# Revit family: SBS20BL
name_source: partatom
category: Generic Models
units: mm (PartAtom-declared; Revit-internal decimal feet)

## family parameters
Always vertical = No
Can host rebar = No
Cut with Voids When Loaded = No
Part Type = Normal
Room Calculation Point = No
Round Connector Dimension = Use Diameter
Shared = No
Work Plane-Based = Yes

## types (1)
- NBS Standard Parameters
    BIMObjectName = Metpro_metprolibrary_conduitfittings_metalcomponent_steelaccessories
    Default Elevation = 1219 mm
    Description = SBS20B - 20mm Spacer Bar Saddle
    DurationUnit = year
    Finish = Black
    ManufacturerName = Metpro Ltd
    ManufacturerURL = www.metpro.co.uk
    Material = Pressed Steel
    ModelReference = SBS20BL
    NBSDescription = Conduit Fittings
    NBSReference = 90-55-10/460
    NominalHeight = 23 mm  [stored 0.0754593 ft]
    NominalLength = 57 mm  [stored 0.187008 ft]
    NominalWidth = 22 mm  [stored 0.0721785 ft]
    ProductInformation = www.metpro.co.uk/pdf/sbs20bl.pdf
    Size = 20mm
    Uniclass2 = Pr_65_70_11_20
    Version = 1
    WarrantyDurationUnit = 1 year
    Weight = 0.0205Kg

note: [stored X ft] marks values corroborated as IEEE doubles in the binary element streams (Revit-internal decimal feet)

## geometry (parser evidence)
native form markers: Sweep x2
no freeform markers — native parametric forms only
